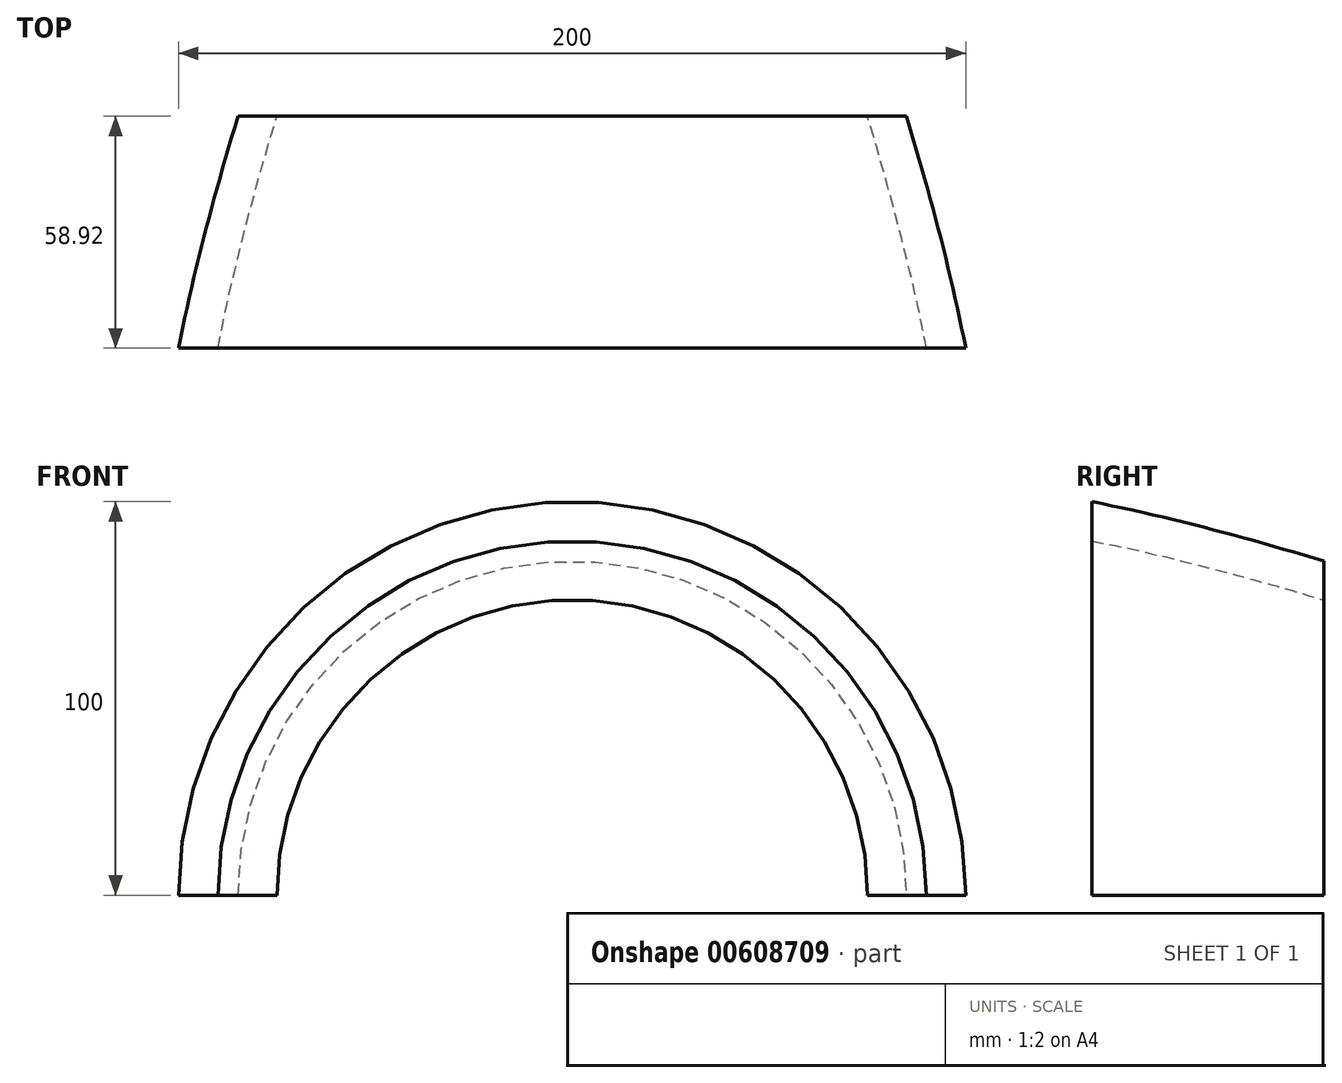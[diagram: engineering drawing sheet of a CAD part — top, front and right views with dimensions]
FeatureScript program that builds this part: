
annotation { "Feature Type Name" : "Feature", "Feature Type Description" : "" }
export const myFeature = defineFeature(function(context is Context, id is Id, definition is map)
    precondition{}
    {
        {
            var Q0;
            Q0=qCreatedBy(makeId("Top.planeOp"),FACE);
            var sketch = newSketch(context, id + "F0", { "sketchPlane" : qUnion([Q0])});
            skLineSegment(sketch, "E0", {"start": v(-41.9, 69.17) * mm, "end": v(-15.02, 69.17) * mm});
            skFitSpline(sketch, "E1.MirrorCS", {"points": [v(58.1, -130.83) * mm, v(33.02, -40.81) * mm, v(-15.02, 69.17) * mm], "startDerivative": vector(-37.24, 187.97) * mm, "endDerivative": vector(-108.84, 150.34) * mm});
            skLineSegment(sketch, "E2.2", {"start": v(-41.9, 59.17) * mm, "end": v(-20.25, 59.17) * mm});
            skFitSpline(sketch, "E2.3", {"points": [v(48.58, -133.2) * mm, v(47.05, -125.5) * mm, v(44.54, -114.08) * mm, v(40.7, -98.72) * mm, v(37.53, -87.04) * mm, v(34.09, -75.1) * mm, v(30.97, -64.87) * mm, v(28.32, -56.47) * mm, v(26.25, -50.05) * mm, v(24.1, -43.5) * mm, v(21.86, -36.8) * mm, v(19.55, -30.01) * mm, v(16.37, -20.86) * mm, v(12.2, -9.31) * mm, v(6.92, 4.47) * mm, v(-0.47, 22.4) * mm, v(-8.35, 39.15) * mm, v(-16.57, 53.66) * mm, v(-20.74, 60) * mm, v(-22.83, 62.88) * mm]});
            skLineSegment(sketch, "E3", {"start": v(-41.9, 69.17) * mm, "end": v(-41.9, 59.17) * mm});
            skLineSegment(sketch, "E4", {"start": v(58.1, -130.83) * mm, "end": v(48.1, -130.83) * mm});
            skLineSegment(sketch, "E5", {"start": v(-41.9, 59.17) * mm, "end": v(-41.9, -63.19) * mm});
            skLineSegment(sketch, "E6", {"start": v(-41.9, -71.91) * mm, "end": v(33.1, -71.91) * mm});
            skLineSegment(sketch, "E7", {"start": v(33.1, -71.91) * mm, "end": v(42.99, -71.91) * mm});
            skSolve(sketch);
        }
        {
            var Q0;
            Q0=makeQuery(id+"F0.imprint","IMPRINT",FACE,{"disambiguationData":[TD([[makeQuery(id+"F0.imprint","IMPRINT",EDGE,{"derivedFrom":sQuery(id+"F0.wireOp",EDGE,"E0")}),-1.0]])]});
            var Q1;
            {var subQ0=sQuery(id+"F0.wireOp",EDGE,"E4");Q1=makeQuery(id+"F0.imprint","IMPRINT",FACE,{"disambiguationData":[TD([[makeQuery(id+"F0.imprint","IMPRINT",EDGE,{"derivedFrom":subQ0}),-1.0]])]});}
            var Q2;
            Q2=sQuery(id+"F0.wireOp",EDGE,"E5");
            revolve(context, id + "F1", {"entities" : qUnion([Q0, Q1]), "axis" : qUnion([Q2]), "revolveType" : RevolveType.ONE_DIRECTION, "angle" : 180 * degree});
        }
    });
